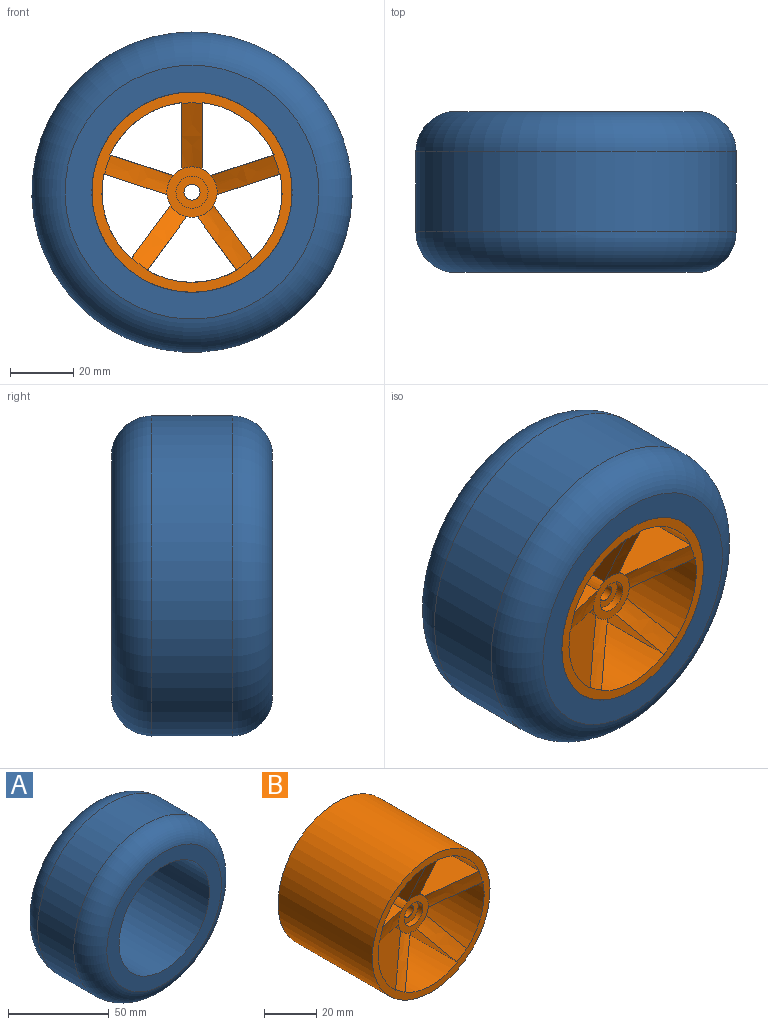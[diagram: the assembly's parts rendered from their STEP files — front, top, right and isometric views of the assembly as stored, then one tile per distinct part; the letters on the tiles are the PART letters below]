
ASSEMBLY  parts=2 mates=1
PART A: 6 faces, bbox 110x51.2x110 mm
  f0: cylinder r=31.75mm len=63.5mm, axis (0,1,0), area 10134.1mm2, adj f1,f5
  f1: plane 80.55x80.55mm, normal (0,1,0), area 1928.8mm2, adj f0,f2
  f2: torus R=37.88mm, axis (0,1,0), area 5288.5mm2, adj f1,f3
  f3: cylinder r=50.8mm len=101.6mm, axis (0,1,0), area 8107.3mm2, adj f2,f4
  f4: torus R=37.88mm, axis (0,1,0), area 5288.5mm2, adj f3,f5
  f5: plane 80.55x80.55mm, normal (0,-1,0), area 1928.8mm2, adj f0,f4
PART B: 36 faces, bbox 63.5x50.8x63.5 mm
  f0: cylinder r=2.54mm len=6.99mm, axis (0,1,0), area 111.5mm2, adj f32,f34
  f1: plane 55.98x53.42mm, normal (0,1,0), area 734.6mm2, adj f5,f6,f7,f8,f9,f10,f11,f12
  f2: plane 63.5x63.5mm, normal (0,-1,0), area 609.8mm2, adj f3,f6,f7,f9,f10,f11,f13,f14
  f3: cylinder r=31.75mm len=63.5mm, axis (0,1,0), area 10134.1mm2, adj f2,f33
  f4: plane 16x16mm, normal (0,-1,0), area 120mm2, adj f5,f8,f12,f15,f18,f21,f22,f23
  f5: cylinder r=8mm len=15.88mm, axis (0,-1,0), area 55.9mm2, adj f1,f4,f6,f7
  f6: plane 25.4x20.02mm, normal (-0.31,0,-0.95), area 434.8mm2, adj f1,f2,f5,f20,f21
  f7: plane 25.4x17.03mm, normal (-0.81,0,0.59), area 434.8mm2, adj f1,f2,f5,f20,f25
  f8: cylinder r=8mm len=15.88mm, axis (0,-1,0), area 55.9mm2, adj f1,f4,f9,f10
  f9: plane 25.4x17.03mm, normal (0.81,0,0.59), area 434.8mm2, adj f1,f2,f8,f20,f24
  f10: plane 25.4x20.02mm, normal (0.31,0,-0.95), area 434.8mm2, adj f1,f2,f8,f20,f23
  f11: plane 25.4x17.03mm, normal (-0.81,0,-0.59), area 434.8mm2, adj f1,f2,f12,f20,f24
  f12: cylinder r=8mm len=15.88mm, axis (0,-1,0), area 55.9mm2, adj f1,f4,f11,f13
  f13: plane 25.4x17.03mm, normal (0.81,0,-0.59), area 434.8mm2, adj f1,f2,f12,f20,f25
  f14: plane 25.4x21.06mm, normal (1,0,0), area 434.8mm2, adj f1,f2,f15,f20,f22
  f15: cylinder r=8mm len=15.88mm, axis (0,-1,0), area 55.9mm2, adj f1,f4,f14,f16
  f16: plane 25.4x20.02mm, normal (-0.31,0,0.95), area 434.8mm2, adj f1,f2,f15,f20,f23
  f17: plane 25.4x20.02mm, normal (0.31,0,0.95), area 434.8mm2, adj f1,f2,f18,f20,f21
  f18: cylinder r=8mm len=15.88mm, axis (0,-1,0), area 55.9mm2, adj f1,f4,f17,f19
  f19: plane 25.4x21.06mm, normal (-1,0,0), area 434.8mm2, adj f1,f2,f18,f20,f22
  f20: cylinder r=28.57mm len=57.15mm, axis (0,-1,0), area 8312.6mm2, adj f1,f2,f6,f7,f9,f10,f11,f13
  f21: cone r=8mm half-angle=64.9deg, axis (0,-1,0), area 143.6mm2, adj f2,f4,f6,f17
  f22: cone r=8mm half-angle=64.9deg, axis (0,-1,0), area 143.6mm2, adj f2,f4,f14,f19
  f23: cone r=8mm half-angle=64.9deg, axis (0,-1,0), area 143.6mm2, adj f2,f4,f10,f16
  f24: cone r=8mm half-angle=64.9deg, axis (0,-1,0), area 143.6mm2, adj f2,f4,f9,f11
  f25: cone r=8mm half-angle=64.9deg, axis (0,-1,0), area 143.6mm2, adj f2,f4,f7,f13
  f26: plane 6.35x6mm, normal (0.87,0,0.5), area 44mm2, adj f1,f27,f31,f32
  f27: plane 6.35x6mm, normal (0.87,0,-0.5), area 44mm2, adj f1,f26,f28,f32
  f28: plane 6.93x6.35mm, normal (0,0,-1), area 44mm2, adj f1,f27,f29,f32
  f29: plane 6.35x6mm, normal (-0.87,0,-0.5), area 44mm2, adj f1,f28,f30,f32
  f30: plane 6.35x6mm, normal (-0.87,0,0.5), area 44mm2, adj f1,f29,f31,f32
  f31: plane 6.93x6.35mm, normal (0,0,1), area 44mm2, adj f1,f26,f30,f32
  f32: plane 13.86x12mm, normal (0,1,0), area 104.4mm2, adj f0,f26,f27,f28,f29,f30,f31
  f33: plane 63.5x63.5mm, normal (0,1,0), area 601.7mm2, adj f3,f20
  f34: plane 10.16x10.16mm, normal (0,-1,0), area 60.8mm2, adj f0,f35
  f35: cylinder r=5.08mm len=10.16mm, axis (0,-1,0), area 81.1mm2, adj f4,f34
PLACE A t=(8.44,-24.18,-45.97)mm
PLACE B t=(8.44,-36.88,-45.97)mm
MATE fastened B.f3 <-> A.f0  axis (0,-1,0) through (8.44,-49.58,-45.97)mm
